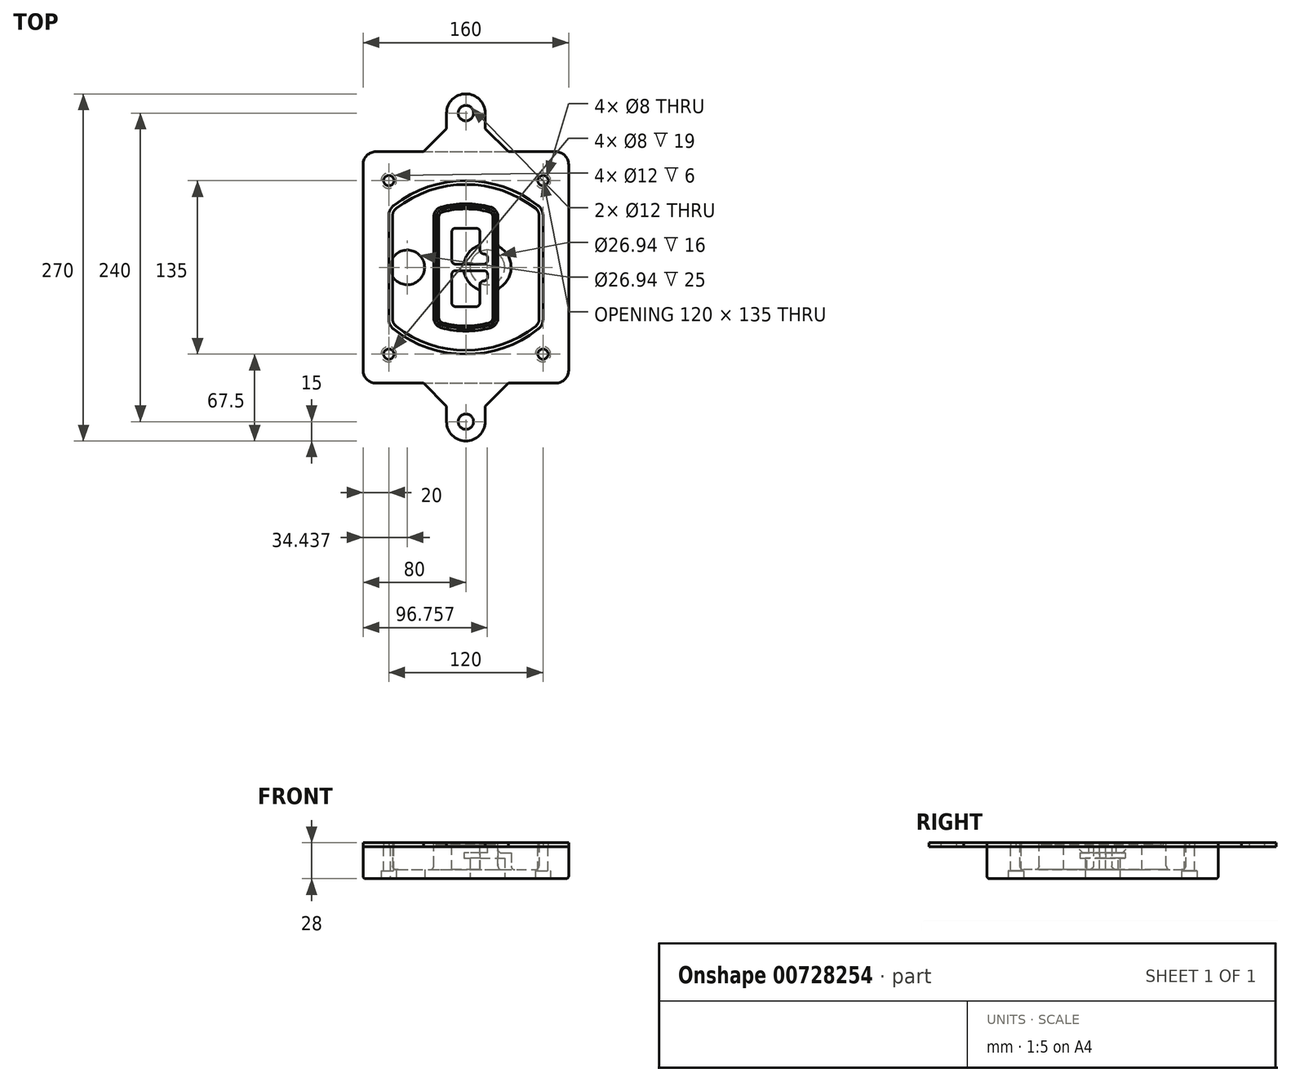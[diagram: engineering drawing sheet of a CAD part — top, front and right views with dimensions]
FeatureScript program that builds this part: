
annotation { "Feature Type Name" : "Feature", "Feature Type Description" : "" }
export const myFeature = defineFeature(function(context is Context, id is Id, definition is map)
    precondition{}
    {
        {
            var Q0;
            Q0=qCreatedBy(makeId("Top.planeOp"),FACE);
            var sketch = newSketch(context, id + "F0", { "sketchPlane" : qUnion([Q0])});
            skPoint(sketch, "E0.rect.middle", {"position": v(0, 0) * mm});
            skLineSegment(sketch, "E1.bottom", {"start": v(-70, -90) * mm, "end": v(70, -90) * mm});
            skLineSegment(sketch, "E1.top", {"start": v(-70, 90) * mm, "end": v(70, 90) * mm});
            skLineSegment(sketch, "E1.left", {"start": v(-80, -80) * mm, "end": v(-80, 80) * mm});
            skLineSegment(sketch, "E1.right", {"start": v(80, -80) * mm, "end": v(80, 80) * mm});
            skLineSegment(sketch, "E2", {"start": v(-80, 90) * mm, "end": v(80, -90) * mm, "construction": true});
            skLineSegment(sketch, "E3", {"start": v(80, 90) * mm, "end": v(-80, -90) * mm, "construction": true});
            skCircle(sketch, "E4", {"center": v(-60, 67.5) * mm, "radius": 4 * mm});
            skCircle(sketch, "E5", {"center": v(60, 67.5) * mm, "radius": 4 * mm});
            skCircle(sketch, "E6", {"center": v(60, -67.5) * mm, "radius": 4 * mm});
            skCircle(sketch, "E7", {"center": v(-60, -67.5) * mm, "radius": 4 * mm});
            skLineSegment(sketch, "E8", {"start": v(-60, 67.5) * mm, "end": v(60, 67.5) * mm, "construction": true});
            skLineSegment(sketch, "E9", {"start": v(60, 67.5) * mm, "end": v(60, -67.5) * mm, "construction": true});
            skLineSegment(sketch, "E10", {"start": v(60, -67.5) * mm, "end": v(-60, -67.5) * mm, "construction": true});
            skLineSegment(sketch, "E11", {"start": v(-60, -67.5) * mm, "end": v(-60, 67.5) * mm, "construction": true});
            skLineSegment(sketch, "E12", {"start": v(-60, 40.3) * mm, "end": v(-60, -40.3) * mm});
            skLineSegment(sketch, "E13", {"start": v(60, 40.3) * mm, "end": v(60, -40.3) * mm});
            skArc(sketch, "E14", {"start": v(56.15, 48.18) * mm, "mid": v(0, 67.5) * mm, "end": v(-56.15, 48.18) * mm});
            skArc(sketch, "E15", {"start": v(-56.15, -48.18) * mm, "mid": v(0, -67.5) * mm, "end": v(56.15, -48.18) * mm});
            skLineSegment(sketch, "E16", {"start": v(-60, 0) * mm, "end": v(60, 0) * mm, "construction": true});
            skPoint(sketch, "E17.visualSharp", {"position": v(-60, -45) * mm});
            skArc(sketch, "E17.filletArc", {"start": v(-60, -40.3) * mm, "mid": v(-58.99, -44.68) * mm, "end": v(-56.15, -48.18) * mm});
            skPoint(sketch, "E18.visualSharp", {"position": v(-60, 45) * mm});
            skArc(sketch, "E18.filletArc", {"start": v(-56.15, 48.18) * mm, "mid": v(-58.99, 44.68) * mm, "end": v(-60, 40.3) * mm});
            skPoint(sketch, "E19.visualSharp", {"position": v(60, 45) * mm});
            skArc(sketch, "E19.filletArc", {"start": v(60, 40.3) * mm, "mid": v(58.99, 44.68) * mm, "end": v(56.15, 48.18) * mm});
            skPoint(sketch, "E20.visualSharp", {"position": v(60, -45) * mm});
            skArc(sketch, "E20.filletArc", {"start": v(56.15, -48.18) * mm, "mid": v(58.99, -44.68) * mm, "end": v(60, -40.3) * mm});
            skPoint(sketch, "E21.visualSharp", {"position": v(-80, 90) * mm});
            skArc(sketch, "E21.filletArc", {"start": v(-70, 90) * mm, "mid": v(-77.07, 87.07) * mm, "end": v(-80, 80) * mm});
            skPoint(sketch, "E22.visualSharp", {"position": v(80, 90) * mm});
            skArc(sketch, "E22.filletArc", {"start": v(80, 80) * mm, "mid": v(77.07, 87.07) * mm, "end": v(70, 90) * mm});
            skPoint(sketch, "E23.visualSharp", {"position": v(80, -90) * mm});
            skArc(sketch, "E23.filletArc", {"start": v(70, -90) * mm, "mid": v(77.07, -87.07) * mm, "end": v(80, -80) * mm});
            skPoint(sketch, "E24.visualSharp", {"position": v(-80, -90) * mm});
            skArc(sketch, "E24.filletArc", {"start": v(-80, -80) * mm, "mid": v(-77.07, -87.07) * mm, "end": v(-70, -90) * mm});
            skArc(sketch, "E25.0", {"start": v(57, 40.3) * mm, "mid": v(56.3, 43.36) * mm, "end": v(54.3, 45.81) * mm});
            skLineSegment(sketch, "E25.1", {"start": v(57, 40.3) * mm, "end": v(57, -40.3) * mm});
            skArc(sketch, "E25.2", {"start": v(54.3, -45.81) * mm, "mid": v(56.3, -43.36) * mm, "end": v(57, -40.3) * mm});
            skArc(sketch, "E25.3", {"start": v(-54.3, -45.81) * mm, "mid": v(0, -64.5) * mm, "end": v(54.3, -45.81) * mm});
            skArc(sketch, "E25.4", {"start": v(-57, -40.3) * mm, "mid": v(-56.3, -43.36) * mm, "end": v(-54.3, -45.81) * mm});
            skArc(sketch, "E25.5", {"start": v(54.3, 45.81) * mm, "mid": v(0, 64.5) * mm, "end": v(-54.3, 45.81) * mm});
            skLineSegment(sketch, "E25.6", {"start": v(-57, 40.3) * mm, "end": v(-57, -40.3) * mm});
            skArc(sketch, "E25.7", {"start": v(-54.3, 45.81) * mm, "mid": v(-56.3, 43.36) * mm, "end": v(-57, 40.3) * mm});
            skArc(sketch, "E26.0", {"start": v(-58.62, 51.33) * mm, "mid": v(-62.58, 46.43) * mm, "end": v(-64, 40.3) * mm});
            skArc(sketch, "E26.1", {"start": v(58.62, 51.33) * mm, "mid": v(0, 71.5) * mm, "end": v(-58.62, 51.33) * mm});
            skArc(sketch, "E26.2", {"start": v(64, 40.3) * mm, "mid": v(62.58, 46.43) * mm, "end": v(58.62, 51.33) * mm});
            skLineSegment(sketch, "E26.3", {"start": v(64, 40.3) * mm, "end": v(64, -40.3) * mm});
            skArc(sketch, "E26.4", {"start": v(58.62, -51.33) * mm, "mid": v(62.58, -46.43) * mm, "end": v(64, -40.3) * mm});
            skLineSegment(sketch, "E26.5", {"start": v(-64, 40.3) * mm, "end": v(-64, -40.3) * mm});
            skArc(sketch, "E26.6", {"start": v(-58.62, -51.33) * mm, "mid": v(0, -71.5) * mm, "end": v(58.62, -51.33) * mm});
            skArc(sketch, "E26.7", {"start": v(-64, -40.3) * mm, "mid": v(-62.58, -46.43) * mm, "end": v(-58.62, -51.33) * mm});
            skSolve(sketch);
        }
        {
            var Q0;
            Q0=makeQuery(id+"F0.imprint","IMPRINT",FACE,{"disambiguationData":[TD([[makeQuery(id+"F0.imprint","IMPRINT",EDGE,{"derivedFrom":sQuery(id+"F0.wireOp",EDGE,"E1.bottom")}),1.0]])]});
            var Q1;
            Q1=makeQuery(id+"F0.imprint","IMPRINT",FACE,{"disambiguationData":[TD([[makeQuery(id+"F0.imprint","IMPRINT",EDGE,{"derivedFrom":sQuery(id+"F0.wireOp",EDGE,"E12")}),1.0]])]});
            var Q2;
            Q2=makeQuery(id+"F0.imprint","IMPRINT",FACE,{"disambiguationData":[TD([[makeQuery(id+"F0.imprint","IMPRINT",EDGE,{"derivedFrom":sQuery(id+"F0.wireOp",EDGE,"E25.0")}),1.0]])]});
            var Q3;
            Q3=makeQuery(id+"F0.imprint","IMPRINT",FACE,{"disambiguationData":[TD([[makeQuery(id+"F0.imprint","IMPRINT",EDGE,{"derivedFrom":sQuery(id+"F0.wireOp",EDGE,"E12")}),-1.0]])]});
            extrude(context, id + "F1", {"entities" : qUnion([Q0, Q1, Q2, Q3]), "oppositeDirection" : true, "depth" : 25 * mm});
        }
        {
            var Q0;
            Q0=makeQuery(id+"F0.imprint","IMPRINT",FACE,{"disambiguationData":[TD([[makeQuery(id+"F0.imprint","IMPRINT",EDGE,{"derivedFrom":sQuery(id+"F0.wireOp",EDGE,"E12")}),1.0]])]});
            extrude(context, id + "F2", {"entities" : qUnion([Q0]), "operationType" : NewBodyOperationType.ADD, "depth" : 3 * mm});
        }
        {
            var Q0;
            Q0=makeQuery(id+"F0.imprint","IMPRINT",FACE,{"disambiguationData":[TD([[makeQuery(id+"F0.imprint","IMPRINT",EDGE,{"derivedFrom":sQuery(id+"F0.wireOp",EDGE,"E25.0")}),1.0]])]});
            extrude(context, id + "F3", {"entities" : qUnion([Q0]), "operationType" : NewBodyOperationType.REMOVE, "oppositeDirection" : true, "depth" : 18 * mm});
        }
        {
            var Q0;
            Q0=makeQuery(id+"F2.opExtrude","CAP_FACE",FACE,{"disambiguationData":[OSD([sQuery(id+"F0.wireOp",EDGE,"E12"),sQuery(id+"F0.wireOp",EDGE,"E13"),sQuery(id+"F0.wireOp",EDGE,"E14"),sQuery(id+"F0.wireOp",EDGE,"E15"),sQuery(id+"F0.wireOp",EDGE,"E17.filletArc"),sQuery(id+"F0.wireOp",EDGE,"E18.filletArc"),sQuery(id+"F0.wireOp",EDGE,"E19.filletArc"),sQuery(id+"F0.wireOp",EDGE,"E20.filletArc"),sQuery(id+"F0.wireOp",EDGE,"E25.0"),sQuery(id+"F0.wireOp",EDGE,"E25.1"),sQuery(id+"F0.wireOp",EDGE,"E25.2"),sQuery(id+"F0.wireOp",EDGE,"E25.3"),sQuery(id+"F0.wireOp",EDGE,"E25.4"),sQuery(id+"F0.wireOp",EDGE,"E25.5"),sQuery(id+"F0.wireOp",EDGE,"E25.6"),sQuery(id+"F0.wireOp",EDGE,"E25.7")])],"isStart":false});
            var sketch = newSketch(context, id + "F4", { "sketchPlane" : qUnion([Q0])});
            skArc(sketch, "E27.0", {"start": v(-19.08, -46.97) * mm, "mid": v(0, -49.5) * mm, "end": v(19.08, -46.97) * mm});
            skArc(sketch, "E28.0", {"start": v(19.08, 46.97) * mm, "mid": v(0, 49.5) * mm, "end": v(-19.08, 46.97) * mm});
            skLineSegment(sketch, "E29", {"start": v(-25, 39.25) * mm, "end": v(-25, -39.25) * mm});
            skLineSegment(sketch, "E30", {"start": v(25, 39.25) * mm, "end": v(25, -39.25) * mm});
            skLineSegment(sketch, "E31", {"start": v(-25, 45.1) * mm, "end": v(25, 45.1) * mm, "construction": true});
            skLineSegment(sketch, "E32", {"start": v(-25, -45.1) * mm, "end": v(25, -45.1) * mm, "construction": true});
            skPoint(sketch, "E33.visualSharp", {"position": v(-25, 45.1) * mm});
            skArc(sketch, "E33.filletArc", {"start": v(-19.08, 46.97) * mm, "mid": v(-23.35, 44.11) * mm, "end": v(-25, 39.25) * mm});
            skPoint(sketch, "E34.visualSharp", {"position": v(25, 45.1) * mm});
            skArc(sketch, "E34.filletArc", {"start": v(25, 39.25) * mm, "mid": v(23.35, 44.11) * mm, "end": v(19.08, 46.97) * mm});
            skPoint(sketch, "E35.visualSharp", {"position": v(25, -45.1) * mm});
            skArc(sketch, "E35.filletArc", {"start": v(19.08, -46.97) * mm, "mid": v(23.35, -44.11) * mm, "end": v(25, -39.25) * mm});
            skPoint(sketch, "E36.visualSharp", {"position": v(-25, -45.1) * mm});
            skArc(sketch, "E36.filletArc", {"start": v(-25, -39.25) * mm, "mid": v(-23.35, -44.11) * mm, "end": v(-19.08, -46.97) * mm});
            skArc(sketch, "E37.0", {"start": v(54.3, 45.81) * mm, "mid": v(0, 64.5) * mm, "end": v(-54.3, 45.81) * mm});
            skArc(sketch, "E37.1", {"start": v(-54.3, 45.81) * mm, "mid": v(-56.3, 43.36) * mm, "end": v(-57, 40.3) * mm});
            skLineSegment(sketch, "E37.2", {"start": v(-57, 40.3) * mm, "end": v(-57, -40.3) * mm});
            skArc(sketch, "E37.3", {"start": v(-57, -40.3) * mm, "mid": v(-56.3, -43.36) * mm, "end": v(-54.3, -45.81) * mm});
            skArc(sketch, "E37.4", {"start": v(-54.3, -45.81) * mm, "mid": v(0, -64.5) * mm, "end": v(54.3, -45.81) * mm});
            skArc(sketch, "E37.5", {"start": v(54.3, -45.81) * mm, "mid": v(56.3, -43.36) * mm, "end": v(57, -40.3) * mm});
            skLineSegment(sketch, "E37.6", {"start": v(57, 40.3) * mm, "end": v(57, -40.3) * mm});
            skArc(sketch, "E37.7", {"start": v(57, 40.3) * mm, "mid": v(56.3, 43.36) * mm, "end": v(54.3, 45.81) * mm});
            skLineSegment(sketch, "E38.0", {"start": v(23, 39.25) * mm, "end": v(23, -39.25) * mm});
            skArc(sketch, "E38.1", {"start": v(18.56, -45.04) * mm, "mid": v(21.76, -42.9) * mm, "end": v(23, -39.25) * mm});
            skArc(sketch, "E38.2", {"start": v(-18.56, -45.04) * mm, "mid": v(0, -47.5) * mm, "end": v(18.56, -45.04) * mm});
            skArc(sketch, "E38.3", {"start": v(-23, -39.25) * mm, "mid": v(-21.76, -42.9) * mm, "end": v(-18.56, -45.04) * mm});
            skLineSegment(sketch, "E38.4", {"start": v(-23, 39.25) * mm, "end": v(-23, -39.25) * mm});
            skArc(sketch, "E38.5", {"start": v(23, 39.25) * mm, "mid": v(21.76, 42.9) * mm, "end": v(18.56, 45.04) * mm});
            skArc(sketch, "E38.6", {"start": v(-18.56, 45.04) * mm, "mid": v(-21.76, 42.9) * mm, "end": v(-23, 39.25) * mm});
            skArc(sketch, "E38.7", {"start": v(18.56, 45.04) * mm, "mid": v(0, 47.5) * mm, "end": v(-18.56, 45.04) * mm});
            skArc(sketch, "E39.0", {"start": v(21, 39.25) * mm, "mid": v(20.18, 41.68) * mm, "end": v(18.04, 43.1) * mm});
            skLineSegment(sketch, "E39.1", {"start": v(21, 39.25) * mm, "end": v(21, -39.25) * mm});
            skArc(sketch, "E39.2", {"start": v(18.04, -43.1) * mm, "mid": v(20.18, -41.68) * mm, "end": v(21, -39.25) * mm});
            skArc(sketch, "E39.3", {"start": v(-18.04, -43.1) * mm, "mid": v(0, -45.5) * mm, "end": v(18.04, -43.1) * mm});
            skArc(sketch, "E39.4", {"start": v(-21, -39.25) * mm, "mid": v(-20.18, -41.68) * mm, "end": v(-18.04, -43.1) * mm});
            skArc(sketch, "E39.5", {"start": v(18.04, 43.1) * mm, "mid": v(0, 45.5) * mm, "end": v(-18.04, 43.1) * mm});
            skLineSegment(sketch, "E39.6", {"start": v(-21, 39.25) * mm, "end": v(-21, -39.25) * mm});
            skArc(sketch, "E39.7", {"start": v(-18.04, 43.1) * mm, "mid": v(-20.18, 41.68) * mm, "end": v(-21, 39.25) * mm});
            skLineSegment(sketch, "E40", {"start": v(-25, 0) * mm, "end": v(25, 0) * mm, "construction": true});
            skLineSegment(sketch, "E41", {"start": v(-11, 5.5) * mm, "end": v(-11, 27.5) * mm});
            skLineSegment(sketch, "E42", {"start": v(-8, 30.5) * mm, "end": v(8, 30.5) * mm});
            skLineSegment(sketch, "E43", {"start": v(11, 27.5) * mm, "end": v(11, 13.5) * mm});
            skLineSegment(sketch, "E44", {"start": v(14, 10.5) * mm, "end": v(14, 10.5) * mm});
            skLineSegment(sketch, "E45", {"start": v(17, 7.5) * mm, "end": v(17, 5.5) * mm});
            skLineSegment(sketch, "E46", {"start": v(14, 2.5) * mm, "end": v(-8, 2.5) * mm});
            skPoint(sketch, "E47.visualSharp", {"position": v(-11, 30.5) * mm});
            skArc(sketch, "E47.filletArc", {"start": v(-8, 30.5) * mm, "mid": v(-10.12, 29.62) * mm, "end": v(-11, 27.5) * mm});
            skPoint(sketch, "E48.visualSharp", {"position": v(11, 30.5) * mm});
            skArc(sketch, "E48.filletArc", {"start": v(11, 27.5) * mm, "mid": v(10.12, 29.62) * mm, "end": v(8, 30.5) * mm});
            skPoint(sketch, "E49.visualSharp", {"position": v(11, 10.5) * mm});
            skArc(sketch, "E49.filletArc", {"start": v(11, 13.5) * mm, "mid": v(11.88, 11.38) * mm, "end": v(14, 10.5) * mm});
            skPoint(sketch, "E50.visualSharp", {"position": v(17, 10.5) * mm});
            skArc(sketch, "E50.filletArc", {"start": v(17, 7.5) * mm, "mid": v(16.12, 9.62) * mm, "end": v(14, 10.5) * mm});
            skPoint(sketch, "E51.visualSharp", {"position": v(17, 2.5) * mm});
            skArc(sketch, "E51.filletArc", {"start": v(14, 2.5) * mm, "mid": v(16.12, 3.38) * mm, "end": v(17, 5.5) * mm});
            skPoint(sketch, "E52.visualSharp", {"position": v(-11, 2.5) * mm});
            skArc(sketch, "E52.filletArc", {"start": v(-11, 5.5) * mm, "mid": v(-10.12, 3.38) * mm, "end": v(-8, 2.5) * mm});
            skLineSegment(sketch, "E53.0.MirrorCS", {"start": v(14, -2.5) * mm, "end": v(-8, -2.5) * mm});
            skArc(sketch, "E54.0.MirrorCS", {"start": v(-11, -5.5) * mm, "mid": v(-10.12, -3.38) * mm, "end": v(-8, -2.5) * mm});
            skLineSegment(sketch, "E55.0.MirrorCS", {"start": v(-11, -5.5) * mm, "end": v(-11, -27.5) * mm});
            skArc(sketch, "E56.0.MirrorCS", {"start": v(-8, -30.5) * mm, "mid": v(-10.12, -29.62) * mm, "end": v(-11, -27.5) * mm});
            skLineSegment(sketch, "E57.0.MirrorCS", {"start": v(-8, -30.5) * mm, "end": v(8, -30.5) * mm});
            skArc(sketch, "E58.0.MirrorCS", {"start": v(11, -27.5) * mm, "mid": v(10.12, -29.62) * mm, "end": v(8, -30.5) * mm});
            skLineSegment(sketch, "E59.0.MirrorCS", {"start": v(11, -27.5) * mm, "end": v(11, -13.5) * mm});
            skArc(sketch, "E60.0.MirrorCS", {"start": v(11, -13.5) * mm, "mid": v(11.88, -11.38) * mm, "end": v(14, -10.5) * mm});
            skArc(sketch, "E61.0.MirrorCS", {"start": v(17, -7.5) * mm, "mid": v(16.12, -9.62) * mm, "end": v(14, -10.5) * mm});
            skLineSegment(sketch, "E62.0.MirrorCS", {"start": v(17, -7.5) * mm, "end": v(17, -5.5) * mm});
            skArc(sketch, "E63.0.MirrorCS", {"start": v(14, -2.5) * mm, "mid": v(16.12, -3.38) * mm, "end": v(17, -5.5) * mm});
            skSolve(sketch);
        }
        {
            var Q0;
            Q0=makeQuery(id+"F4.imprint","IMPRINT",FACE,{"disambiguationData":[TD([[makeQuery(id+"F4.imprint","IMPRINT",EDGE,{"derivedFrom":sQuery(id+"F4.wireOp",EDGE,"E27.0")}),1.0]])]});
            var Q1;
            Q1=makeQuery(id+"F4.imprint","IMPRINT",FACE,{"disambiguationData":[TD([[makeQuery(id+"F4.imprint","IMPRINT",EDGE,{"derivedFrom":sQuery(id+"F4.wireOp",EDGE,"E38.0")}),-1.0]])]});
            var Q2;
            Q2=makeQuery(id+"F4.imprint","IMPRINT",FACE,{"disambiguationData":[TD([[makeQuery(id+"F4.imprint","IMPRINT",EDGE,{"derivedFrom":sQuery(id+"F4.wireOp",EDGE,"E39.0")}),1.0]])]});
            extrude(context, id + "F5", {"entities" : qUnion([Q0, Q1, Q2]), "operationType" : NewBodyOperationType.ADD, "endBound" : BoundingType.UP_TO_NEXT, "oppositeDirection" : true, "depth" : 25 * mm});
        }
        {
            var Q0;
            Q0=makeQuery(id+"F4.imprint","IMPRINT",FACE,{"disambiguationData":[TD([[makeQuery(id+"F4.imprint","IMPRINT",EDGE,{"derivedFrom":sQuery(id+"F4.wireOp",EDGE,"E38.0")}),-1.0]])]});
            extrude(context, id + "F6", {"entities" : qUnion([Q0]), "operationType" : NewBodyOperationType.REMOVE, "oppositeDirection" : true, "depth" : 2 * mm});
        }
        {
            var Q0;
            Q0=makeQuery(id+"F1.opExtrude","CAP_FACE",FACE,{"disambiguationData":[OSD([sQuery(id+"F0.wireOp",EDGE,"E1.bottom"),sQuery(id+"F0.wireOp",EDGE,"E1.top"),sQuery(id+"F0.wireOp",EDGE,"E1.left"),sQuery(id+"F0.wireOp",EDGE,"E1.right"),sQuery(id+"F0.wireOp",EDGE,"E4"),sQuery(id+"F0.wireOp",EDGE,"E5"),sQuery(id+"F0.wireOp",EDGE,"E6"),sQuery(id+"F0.wireOp",EDGE,"E7"),sQuery(id+"F0.wireOp",EDGE,"E21.filletArc"),sQuery(id+"F0.wireOp",EDGE,"E22.filletArc"),sQuery(id+"F0.wireOp",EDGE,"E23.filletArc"),sQuery(id+"F0.wireOp",EDGE,"E24.filletArc")])],"isStart":false});
            var sketch = newSketch(context, id + "F7", { "sketchPlane" : qUnion([Q0])});
            skCircle(sketch, "E64", {"center": v(16.76, 0) * mm, "radius": 13.47 * mm});
            skCircle(sketch, "E65", {"center": v(-45.56, 0) * mm, "radius": 13.47 * mm});
            skLineSegment(sketch, "E66", {"start": v(80, 0) * mm, "end": v(-80, 0) * mm});
            skCircle(sketch, "E67", {"center": v(16.76, 0) * mm, "radius": 18.47 * mm});
            skCircle(sketch, "E68", {"center": v(60, -67.5) * mm, "radius": 6 * mm});
            skCircle(sketch, "E69", {"center": v(-60, -67.5) * mm, "radius": 6 * mm});
            skCircle(sketch, "E70", {"center": v(-60, 67.5) * mm, "radius": 6 * mm});
            skCircle(sketch, "E71", {"center": v(60, 67.5) * mm, "radius": 6 * mm});
            skSolve(sketch);
        }
        {
            var Q0;
            {var subQ1=sQuery(id+"F7.wireOp",EDGE,"E66");var subQ4=sQuery(id+"F7.wireOp",EDGE,"E64");var subQ6=makeQuery(id+"F7.imprint","INTERSECT",VERTEX,{"disambiguationData":[OD(0.0)],"derivedFrom":[subQ4,subQ1]});Q0=makeQuery(id+"F7.imprint","IMPRINT",FACE,{"disambiguationData":[TD([[makeQuery(id+"F7.imprint","IMPRINT",EDGE,{"disambiguationData":[TD([[subQ6,-1.0]])],"derivedFrom":subQ4}),-1.0]])]});}
            var Q1;
            {var subQ0=sQuery(id+"F7.wireOp",EDGE,"E66");var subQ1=sQuery(id+"F7.wireOp",EDGE,"E64");var subQ3=makeQuery(id+"F7.imprint","INTERSECT",VERTEX,{"disambiguationData":[OD(0.0)],"derivedFrom":[subQ1,subQ0]});Q1=makeQuery(id+"F7.imprint","IMPRINT",FACE,{"disambiguationData":[TD([[makeQuery(id+"F7.imprint","IMPRINT",EDGE,{"disambiguationData":[TD([[subQ3,-1.0]])],"derivedFrom":subQ1}),1.0]])]});}
            var Q2;
            {var subQ0=sQuery(id+"F7.wireOp",EDGE,"E66");var subQ1=sQuery(id+"F7.wireOp",EDGE,"E64");var subQ3=makeQuery(id+"F7.imprint","INTERSECT",VERTEX,{"disambiguationData":[OD(0.0)],"derivedFrom":[subQ1,subQ0]});Q2=makeQuery(id+"F7.imprint","IMPRINT",FACE,{"disambiguationData":[TD([[makeQuery(id+"F7.imprint","IMPRINT",EDGE,{"disambiguationData":[TD([[subQ3,1.0]])],"derivedFrom":subQ1}),1.0]])]});}
            var Q3;
            {var subQ1=sQuery(id+"F7.wireOp",EDGE,"E66");var subQ4=sQuery(id+"F7.wireOp",EDGE,"E64");var subQ6=makeQuery(id+"F7.imprint","INTERSECT",VERTEX,{"disambiguationData":[OD(0.0)],"derivedFrom":[subQ4,subQ1]});Q3=makeQuery(id+"F7.imprint","IMPRINT",FACE,{"disambiguationData":[TD([[makeQuery(id+"F7.imprint","IMPRINT",EDGE,{"disambiguationData":[TD([[subQ6,1.0]])],"derivedFrom":subQ4}),-1.0]])]});}
            extrude(context, id + "F8", {"entities" : qUnion([Q0, Q1, Q2, Q3]), "operationType" : NewBodyOperationType.ADD, "oppositeDirection" : true, "depth" : 20 * mm});
        }
        {
            var Q0;
            {var subQ0=sQuery(id+"F7.wireOp",EDGE,"E66");var subQ1=sQuery(id+"F7.wireOp",EDGE,"E64");var subQ3=makeQuery(id+"F7.imprint","INTERSECT",VERTEX,{"disambiguationData":[OD(0.0)],"derivedFrom":[subQ1,subQ0]});Q0=makeQuery(id+"F7.imprint","IMPRINT",FACE,{"disambiguationData":[TD([[makeQuery(id+"F7.imprint","IMPRINT",EDGE,{"disambiguationData":[TD([[subQ3,-1.0]])],"derivedFrom":subQ1}),1.0]])]});}
            var Q1;
            {var subQ0=sQuery(id+"F7.wireOp",EDGE,"E66");var subQ1=sQuery(id+"F7.wireOp",EDGE,"E64");var subQ3=makeQuery(id+"F7.imprint","INTERSECT",VERTEX,{"disambiguationData":[OD(0.0)],"derivedFrom":[subQ1,subQ0]});Q1=makeQuery(id+"F7.imprint","IMPRINT",FACE,{"disambiguationData":[TD([[makeQuery(id+"F7.imprint","IMPRINT",EDGE,{"disambiguationData":[TD([[subQ3,1.0]])],"derivedFrom":subQ1}),1.0]])]});}
            extrude(context, id + "F9", {"entities" : qUnion([Q0, Q1]), "operationType" : NewBodyOperationType.REMOVE, "oppositeDirection" : true, "depth" : 16 * mm});
        }
        {
            var Q0;
            {var subQ0=sQuery(id+"F7.wireOp",EDGE,"E66");var subQ1=sQuery(id+"F7.wireOp",EDGE,"E65");var subQ3=makeQuery(id+"F7.imprint","INTERSECT",VERTEX,{"disambiguationData":[OD(0.0)],"derivedFrom":[subQ1,subQ0]});Q0=makeQuery(id+"F7.imprint","IMPRINT",FACE,{"disambiguationData":[TD([[makeQuery(id+"F7.imprint","IMPRINT",EDGE,{"disambiguationData":[TD([[subQ3,-1.0]])],"derivedFrom":subQ1}),1.0]])]});}
            var Q1;
            {var subQ0=sQuery(id+"F7.wireOp",EDGE,"E66");var subQ1=sQuery(id+"F7.wireOp",EDGE,"E65");var subQ3=makeQuery(id+"F7.imprint","INTERSECT",VERTEX,{"disambiguationData":[OD(0.0)],"derivedFrom":[subQ1,subQ0]});Q1=makeQuery(id+"F7.imprint","IMPRINT",FACE,{"disambiguationData":[TD([[makeQuery(id+"F7.imprint","IMPRINT",EDGE,{"disambiguationData":[TD([[subQ3,1.0]])],"derivedFrom":subQ1}),1.0]])]});}
            extrude(context, id + "F10", {"entities" : qUnion([Q0, Q1]), "operationType" : NewBodyOperationType.REMOVE, "oppositeDirection" : true, "depth" : 25 * mm});
        }
        {
            var Q0;
            Q0=makeQuery(id+"F7.imprint","IMPRINT",FACE,{"disambiguationData":[TD([[makeQuery(id+"F7.imprint","IMPRINT",EDGE,{"derivedFrom":sQuery(id+"F7.wireOp",EDGE,"E68")}),1.0]])]});
            var Q1;
            Q1=makeQuery(id+"F7.imprint","IMPRINT",FACE,{"disambiguationData":[TD([[makeQuery(id+"F7.imprint","IMPRINT",EDGE,{"derivedFrom":makeQuery(id+"F1.opExtrude","CAP_EDGE",EDGE,{"disambiguationData":[OSD([sQuery(id+"F0.wireOp",EDGE,"E5")])],"isStart":false})}),-1.0]])]});
            var Q2;
            Q2=makeQuery(id+"F7.imprint","IMPRINT",FACE,{"disambiguationData":[TD([[makeQuery(id+"F7.imprint","IMPRINT",EDGE,{"derivedFrom":sQuery(id+"F7.wireOp",EDGE,"E69")}),1.0]])]});
            var Q3;
            Q3=makeQuery(id+"F7.imprint","IMPRINT",FACE,{"disambiguationData":[TD([[makeQuery(id+"F7.imprint","IMPRINT",EDGE,{"derivedFrom":makeQuery(id+"F1.opExtrude","CAP_EDGE",EDGE,{"disambiguationData":[OSD([sQuery(id+"F0.wireOp",EDGE,"E4")])],"isStart":false})}),-1.0]])]});
            var Q4;
            Q4=makeQuery(id+"F7.imprint","IMPRINT",FACE,{"disambiguationData":[TD([[makeQuery(id+"F7.imprint","IMPRINT",EDGE,{"derivedFrom":sQuery(id+"F7.wireOp",EDGE,"E70")}),1.0]])]});
            var Q5;
            Q5=makeQuery(id+"F7.imprint","IMPRINT",FACE,{"disambiguationData":[TD([[makeQuery(id+"F7.imprint","IMPRINT",EDGE,{"derivedFrom":makeQuery(id+"F1.opExtrude","CAP_EDGE",EDGE,{"disambiguationData":[OSD([sQuery(id+"F0.wireOp",EDGE,"E7")])],"isStart":false})}),-1.0]])]});
            var Q6;
            Q6=makeQuery(id+"F7.imprint","IMPRINT",FACE,{"disambiguationData":[TD([[makeQuery(id+"F7.imprint","IMPRINT",EDGE,{"derivedFrom":sQuery(id+"F7.wireOp",EDGE,"E71")}),1.0]])]});
            var Q7;
            Q7=makeQuery(id+"F7.imprint","IMPRINT",FACE,{"disambiguationData":[TD([[makeQuery(id+"F7.imprint","IMPRINT",EDGE,{"derivedFrom":makeQuery(id+"F1.opExtrude","CAP_EDGE",EDGE,{"disambiguationData":[OSD([sQuery(id+"F0.wireOp",EDGE,"E6")])],"isStart":false})}),-1.0]])]});
            extrude(context, id + "F11", {"entities" : qUnion([Q0, Q1, Q2, Q3, Q4, Q5, Q6, Q7]), "operationType" : NewBodyOperationType.REMOVE, "oppositeDirection" : true, "depth" : 6 * mm});
        }
        {
            var Q0;
            Q0=makeQuery(id+"F9.boolean.opBoolean","COPY",FACE,{"derivedFrom":makeQuery(id+"F9.opExtrude","CAP_FACE",FACE,{"disambiguationData":[OSD([sQuery(id+"F7.wireOp",EDGE,"E64")])],"isStart":false})});
            var sketch = newSketch(context, id + "F12", { "sketchPlane" : qUnion([Q0])});
            skArc(sketch, "E72.0", {"start": v(11, 17.55) * mm, "mid": v(2.57, 11.82) * mm, "end": v(-1.54, 2.5) * mm});
            skArc(sketch, "E72.1", {"start": v(-1.54, -2.5) * mm, "mid": v(2.57, -11.82) * mm, "end": v(11, -17.55) * mm});
            skLineSegment(sketch, "E73", {"start": v(-1.54, -2.5) * mm, "end": v(14, -2.5) * mm});
            skLineSegment(sketch, "E74.0", {"start": v(14, 2.5) * mm, "end": v(-1.54, 2.5) * mm});
            skArc(sketch, "E74.1", {"start": v(14, 2.5) * mm, "mid": v(16.12, 3.38) * mm, "end": v(17, 5.5) * mm});
            skLineSegment(sketch, "E74.2", {"start": v(17, 7.5) * mm, "end": v(17, 5.5) * mm});
            skArc(sketch, "E74.3", {"start": v(17, 7.5) * mm, "mid": v(16.12, 9.62) * mm, "end": v(14, 10.5) * mm});
            skArc(sketch, "E74.4", {"start": v(11, 13.5) * mm, "mid": v(11.88, 11.38) * mm, "end": v(14, 10.5) * mm});
            skLineSegment(sketch, "E74.5", {"start": v(11, 17.55) * mm, "end": v(11, 13.5) * mm});
            skLineSegment(sketch, "E74.7", {"start": v(14, -2.5) * mm, "end": v(-1.54, -2.5) * mm});
            skArc(sketch, "E74.8", {"start": v(14, -2.5) * mm, "mid": v(16.12, -3.38) * mm, "end": v(17, -5.5) * mm});
            skLineSegment(sketch, "E74.9", {"start": v(17, -7.5) * mm, "end": v(17, -5.5) * mm});
            skArc(sketch, "E74.10", {"start": v(17, -7.5) * mm, "mid": v(16.12, -9.62) * mm, "end": v(14, -10.5) * mm});
            skArc(sketch, "E74.11", {"start": v(11, -13.5) * mm, "mid": v(11.88, -11.38) * mm, "end": v(14, -10.5) * mm});
            skLineSegment(sketch, "E74.12", {"start": v(11, -17.55) * mm, "end": v(11, -13.5) * mm});
            skPoint(sketch, "E75.orphan", {"position": v(11, -27.5) * mm});
            skPoint(sketch, "E76.orphan", {"position": v(-8, -2.5) * mm});
            skPoint(sketch, "E77.orphan", {"position": v(-8, 2.5) * mm});
            skPoint(sketch, "E78.orphan", {"position": v(11, 27.5) * mm});
            skSolve(sketch);
        }
        {
            var Q0;
            {var subQ7=sQuery(id+"F12.wireOp",EDGE,"E72.0");var subQ14=sQuery(id+"F12.wireOp",EDGE,"E72.1");var subQ16=sQuery(id+"F12.wireOp",EDGE,"E74.1");var subQ18=sQuery(id+"F12.wireOp",EDGE,"E74.8");Q0=qUnion([makeQuery(id+"F12.imprint","IMPRINT",FACE,{"disambiguationData":[TD([[makeQuery(id+"F12.imprint","IMPRINT",EDGE,{"derivedFrom":subQ7}),1.0]])]}),makeQuery(id+"F12.imprint","IMPRINT",FACE,{"disambiguationData":[TD([[makeQuery(id+"F12.imprint","IMPRINT",EDGE,{"derivedFrom":subQ14}),1.0]])]}),makeQuery(id+"F12.imprint","IMPRINT",FACE,{"disambiguationData":[TD([[makeQuery(id+"F12.imprint","IMPRINT",EDGE,{"derivedFrom":subQ16}),1.0]])]}),makeQuery(id+"F12.imprint","IMPRINT",FACE,{"disambiguationData":[TD([[makeQuery(id+"F12.imprint","IMPRINT",EDGE,{"derivedFrom":subQ18}),-1.0]])]})]);}
            var Q1;
            Q1=makeQuery(id+"F5.boolean.opBoolean","SPLIT",FACE,{"disambiguationData":[TD([makeQuery(id+"F5.opExtrude","SWEPT_FACE",FACE,{"disambiguationData":[OSD([sQuery(id+"F4.wireOp",EDGE,"E41")])]})])],"derivedFrom":makeQuery(id+"F3.boolean.opBoolean","COPY",FACE,{"derivedFrom":makeQuery(id+"F3.opExtrude","CAP_FACE",FACE,{"disambiguationData":[OSD([sQuery(id+"F0.wireOp",EDGE,"E25.0"),sQuery(id+"F0.wireOp",EDGE,"E25.1"),sQuery(id+"F0.wireOp",EDGE,"E25.2"),sQuery(id+"F0.wireOp",EDGE,"E25.3"),sQuery(id+"F0.wireOp",EDGE,"E25.4"),sQuery(id+"F0.wireOp",EDGE,"E25.5"),sQuery(id+"F0.wireOp",EDGE,"E25.6"),sQuery(id+"F0.wireOp",EDGE,"E25.7")])],"isStart":false})})});
            extrude(context, id + "F13", {"entities" : qUnion([Q0]), "operationType" : NewBodyOperationType.REMOVE, "endBound" : BoundingType.UP_TO_SURFACE, "endBoundEntityFace" : qUnion([Q1]), "depth" : 25 * mm});
        }
        {
            var Q0;
            Q0=makeQuery(id+"F3.boolean.opBoolean","COPY",EDGE,{"derivedFrom":makeQuery(id+"F3.opExtrude","CAP_EDGE",EDGE,{"disambiguationData":[OSD([sQuery(id+"F0.wireOp",EDGE,"E25.6")])],"isStart":false})});
            var Q1;
            Q1=makeQuery(id+"F8.boolean.opBoolean","INTERSECT",EDGE,{"derivedFrom":[makeQuery(id+"F5.opExtrude","SWEPT_FACE",FACE,{"disambiguationData":[OSD([sQuery(id+"F4.wireOp",EDGE,"E30")])]}),makeQuery(id+"F8.opExtrude","CAP_FACE",FACE,{"disambiguationData":[OSD([sQuery(id+"F7.wireOp",EDGE,"E67")])],"isStart":false})]});
            var Q2;
            Q2=makeQuery(id+"F8.boolean.opBoolean","INTERSECT",EDGE,{"disambiguationData":[OD(1.0)],"derivedFrom":[makeQuery(id+"F5.opExtrude","SWEPT_FACE",FACE,{"disambiguationData":[OSD([sQuery(id+"F4.wireOp",EDGE,"E30")])]}),makeQuery(id+"F8.opExtrude","SWEPT_FACE",FACE,{"disambiguationData":[OSD([sQuery(id+"F7.wireOp",EDGE,"E67")])]})]});
            var Q3;
            {var subQ0=sQuery(id+"F4.wireOp",EDGE,"E30");Q3=makeQuery(id+"F8.boolean.opBoolean","SPLIT",EDGE,{"disambiguationData":[TD([makeQuery(id+"F5.opExtrude","SWEPT_FACE",FACE,{"disambiguationData":[OSD([sQuery(id+"F4.wireOp",EDGE,"E35.filletArc")])]})])],"derivedFrom":makeQuery(id+"F5.opExtrude","CAP_EDGE",EDGE,{"disambiguationData":[OSD([subQ0])],"isStart":false})});}
            var Q4;
            {var subQ0=sQuery(id+"F0.wireOp",EDGE,"E25.7");var subQ1=sQuery(id+"F0.wireOp",EDGE,"E25.1");var subQ2=sQuery(id+"F0.wireOp",EDGE,"E25.6");var subQ3=sQuery(id+"F0.wireOp",EDGE,"E25.5");var subQ4=sQuery(id+"F0.wireOp",EDGE,"E25.4");var subQ5=sQuery(id+"F0.wireOp",EDGE,"E25.0");var subQ6=sQuery(id+"F0.wireOp",EDGE,"E25.2");var subQ7=sQuery(id+"F0.wireOp",EDGE,"E25.3");Q4=makeQuery(id+"F8.boolean.opBoolean","INTERSECT",EDGE,{"derivedFrom":[makeQuery(id+"F5.boolean.opBoolean","SPLIT",FACE,{"disambiguationData":[TD([makeQuery(id+"F2.opExtrude","SWEPT_FACE",FACE,{"disambiguationData":[OSD([subQ5])]})])],"derivedFrom":makeQuery(id+"F3.boolean.opBoolean","COPY",FACE,{"derivedFrom":makeQuery(id+"F3.opExtrude","CAP_FACE",FACE,{"disambiguationData":[OSD([subQ5,subQ1,subQ6,subQ7,subQ4,subQ3,subQ2,subQ0])],"isStart":false})})}),makeQuery(id+"F8.opExtrude","SWEPT_FACE",FACE,{"disambiguationData":[OSD([sQuery(id+"F7.wireOp",EDGE,"E67")])]})]});}
            var Q5;
            Q5=makeQuery(id+"F8.boolean.opBoolean","INTERSECT",EDGE,{"disambiguationData":[OD(0.0)],"derivedFrom":[makeQuery(id+"F5.opExtrude","SWEPT_FACE",FACE,{"disambiguationData":[OSD([sQuery(id+"F4.wireOp",EDGE,"E30")])]}),makeQuery(id+"F8.opExtrude","SWEPT_FACE",FACE,{"disambiguationData":[OSD([sQuery(id+"F7.wireOp",EDGE,"E67")])]})]});
            fillet(context, id + "F14", {"entities" : qUnion([Q0, Q1, Q2, Q3, Q4, Q5]), "radius" : 3 * mm, "tangentPropagation" : true, "allowEdgeOverflow" : false});
        }
        {
            var Q0;
            Q0=makeQuery(id+"F1.opExtrude","CAP_EDGE",EDGE,{"disambiguationData":[OSD([sQuery(id+"F0.wireOp",EDGE,"E1.bottom")])],"isStart":false});
            fillet(context, id + "F15", {"entities" : qUnion([Q0]), "radius" : 2 * mm, "tangentPropagation" : true, "allowEdgeOverflow" : false});
        }
        {
            var Q0;
            {var subQ0=sQuery(id+"F0.wireOp",EDGE,"E21.filletArc");var subQ1=sQuery(id+"F0.wireOp",EDGE,"E7");var subQ2=sQuery(id+"F0.wireOp",EDGE,"E6");var subQ3=sQuery(id+"F0.wireOp",EDGE,"E5");var subQ4=sQuery(id+"F0.wireOp",EDGE,"E4");var subQ5=sQuery(id+"F0.wireOp",EDGE,"E22.filletArc");var subQ6=sQuery(id+"F0.wireOp",EDGE,"E1.bottom");var subQ7=sQuery(id+"F0.wireOp",EDGE,"E1.right");var subQ8=sQuery(id+"F0.wireOp",EDGE,"E1.top");var subQ9=sQuery(id+"F0.wireOp",EDGE,"E1.left");var subQ10=sQuery(id+"F0.wireOp",EDGE,"E23.filletArc");var subQ11=sQuery(id+"F0.wireOp",EDGE,"E24.filletArc");Q0=makeQuery(id+"F2.boolean.opBoolean","SPLIT",FACE,{"disambiguationData":[TD([makeQuery(id+"F1.opExtrude","SWEPT_FACE",FACE,{"disambiguationData":[OSD([subQ6])]})])],"derivedFrom":makeQuery(id+"F1.opExtrude","CAP_FACE",FACE,{"disambiguationData":[OSD([subQ6,subQ8,subQ9,subQ7,subQ4,subQ3,subQ2,subQ1,subQ0,subQ5,subQ10,subQ11])],"isStart":true})});}
            var sketch = newSketch(context, id + "F16", { "sketchPlane" : qUnion([Q0])});
            skLineSegment(sketch, "E79", {"start": v(0, 90) * mm, "end": v(0, 120) * mm, "construction": true});
            skCircle(sketch, "E80", {"center": v(0, 120) * mm, "radius": 6 * mm});
            skLineSegment(sketch, "E81", {"start": v(-15, 108) * mm, "end": v(-15, 120) * mm});
            skLineSegment(sketch, "E82", {"start": v(15, 108) * mm, "end": v(15, 120) * mm});
            skArc(sketch, "E83", {"start": v(15, 120) * mm, "mid": v(0, 135) * mm, "end": v(-15, 120) * mm});
            skLineSegment(sketch, "E84", {"start": v(-15, 108) * mm, "end": v(-33, 90) * mm});
            skLineSegment(sketch, "E85", {"start": v(15, 108) * mm, "end": v(33, 90) * mm});
            skLineSegment(sketch, "E86", {"start": v(-80, 0) * mm, "end": v(80, 0) * mm, "construction": true});
            skLineSegment(sketch, "E87.MirrorCS", {"start": v(15, -108) * mm, "end": v(33, -90) * mm});
            skLineSegment(sketch, "E88.MirrorCS", {"start": v(15, -108) * mm, "end": v(15, -120) * mm});
            skArc(sketch, "E89.MirrorCS", {"start": v(15, -120) * mm, "mid": v(0, -135) * mm, "end": v(-15, -120) * mm});
            skLineSegment(sketch, "E90.MirrorCS", {"start": v(-15, -108) * mm, "end": v(-15, -120) * mm});
            skLineSegment(sketch, "E91.MirrorCS", {"start": v(-15, -108) * mm, "end": v(-33, -90) * mm});
            skLineSegment(sketch, "E92.MirrorCS", {"start": v(0, -90) * mm, "end": v(0, -120) * mm, "construction": true});
            skCircle(sketch, "E93.MirrorC", {"center": v(0, -120) * mm, "radius": 6 * mm});
            skSolve(sketch);
        }
        {
            var Q0;
            Q0=makeQuery(id+"F16.imprint","IMPRINT",FACE,{"disambiguationData":[TD([[makeQuery(id+"F16.imprint","IMPRINT",EDGE,{"derivedFrom":sQuery(id+"F16.wireOp",EDGE,"E80")}),-1.0]])]});
            var Q1;
            Q1=makeQuery(id+"F16.imprint","IMPRINT",FACE,{"disambiguationData":[TD([[makeQuery(id+"F16.imprint","IMPRINT",EDGE,{"derivedFrom":makeQuery(id+"F1.opExtrude","CAP_EDGE",EDGE,{"disambiguationData":[OSD([sQuery(id+"F0.wireOp",EDGE,"E1.left")])],"isStart":true})}),-1.0]])]});
            var Q2;
            Q2=makeQuery(id+"F16.imprint","IMPRINT",FACE,{"disambiguationData":[TD([[makeQuery(id+"F16.imprint","IMPRINT",EDGE,{"derivedFrom":sQuery(id+"F16.wireOp",EDGE,"E88.MirrorCS")}),-1.0]])]});
            var Q3;
            Q3=makeQuery(id+"F2.opExtrude","CAP_FACE",FACE,{"disambiguationData":[OSD([sQuery(id+"F0.wireOp",EDGE,"E12"),sQuery(id+"F0.wireOp",EDGE,"E13"),sQuery(id+"F0.wireOp",EDGE,"E14"),sQuery(id+"F0.wireOp",EDGE,"E15"),sQuery(id+"F0.wireOp",EDGE,"E17.filletArc"),sQuery(id+"F0.wireOp",EDGE,"E18.filletArc"),sQuery(id+"F0.wireOp",EDGE,"E19.filletArc"),sQuery(id+"F0.wireOp",EDGE,"E20.filletArc"),sQuery(id+"F0.wireOp",EDGE,"E25.0"),sQuery(id+"F0.wireOp",EDGE,"E25.1"),sQuery(id+"F0.wireOp",EDGE,"E25.2"),sQuery(id+"F0.wireOp",EDGE,"E25.3"),sQuery(id+"F0.wireOp",EDGE,"E25.4"),sQuery(id+"F0.wireOp",EDGE,"E25.5"),sQuery(id+"F0.wireOp",EDGE,"E25.6"),sQuery(id+"F0.wireOp",EDGE,"E25.7")])],"isStart":false});
            extrude(context, id + "F17", {"entities" : qUnion([Q0, Q1, Q2]), "endBound" : BoundingType.UP_TO_SURFACE, "depth" : 25 * mm, "endBoundEntityFace" : qUnion([Q3]), "offsetDistance" : 25 * mm});
        }
    });
